# Revit family: FB-08 - v1.0 20241101 1310 kubota
name_source: partatom
category: Communication Devices
units: mm (PartAtom-declared; Revit-internal decimal feet)

## family parameters
Always vertical = Yes
Cut with Voids When Loaded = No
Maintain Annotation Orientation = No
Part Type = Normal
Room Calculation Point = No
Round Connector Dimension = Use Diameter
Shared = No
Work Plane-Based = Yes

## types (2) — shared parameters
Default Elevation = 1219 mm
Dimensions = 200 (W) X 350 (H) X 400 (D) mm (7.87" X 13.78" X 15.75")
Enclosure = Bass-reflex type
Frequency Response = 45 Hz - 300 Hz, -10 dB at installation in 1/2 free sound field
Input Termina = M4 screw terminal, distance between barriers: 9 mm ( 0.35")
Instollation Environment = Indoor installation
Manufacturer = TOA
Operoting Temperature = -10 °C to +50 °C (14 °F to 122 °F)
Power Handling Capacity = Rated noise power: 120 W (8 Ω), Continuous program: 240 W (8 Ω)
Product Info = https://www.toa-products.com
Rated Impedance (100V line) = 83 Ω (120 W), 167 Ω (60 W)
Rated Impedance (70V line) = 50 Ω (100 W), 83 Ω (60 W), 167 Ω (30 W)
Rated Impedance (Low) = 8 Ω
Rated Input = 120 W (100 V line, 70 V line)
Recommended Amplifiers = DA-250DH, DA-250FH, DA-500FH, A-5012
Sensitivty = 84 dB (1 W, 1 m) at installation in free sound field, 90 dB (1 W, 1 m) at installation in 1/2 free sound field
Speaker Component = 20 cm (8") cone-type
URL = https://www.toa.jp
Update Info = https://www.sound-toa.com
Version = 1.0
Weight = 16 kg (3.53 lb)

## per-type parameters (varying)
| type | Body | Finish - Enclosure | Finish - Grille | Grille | Model | Option |
| FB-08BT | TOA-Body(Black) | MDF, black (RAL 9011 equivalent), paint | Surface treated steel plate, black (RAL 9011 equivalent), paint | TOA-Grille(Black) | FB-08BT
FB-08BT | Subwoofer wall mounting bracket: HY-WM-FB08B, Subwoofer ceiling mounting bracket: HY-CM-FB08B |
| FB-08WT | TOA-Body(White) | MDF, white (RAL 9016 equivalent), paint | Surface treated steel plate, white (RAL 9016 equivalent), paint | TOA-Grille(White) | FB-08WT | Subwoofer wall mounting bracket: HY-WM-FB08W, Subwoofer ceiling mounting bracket: HY-CM-FB08W |
